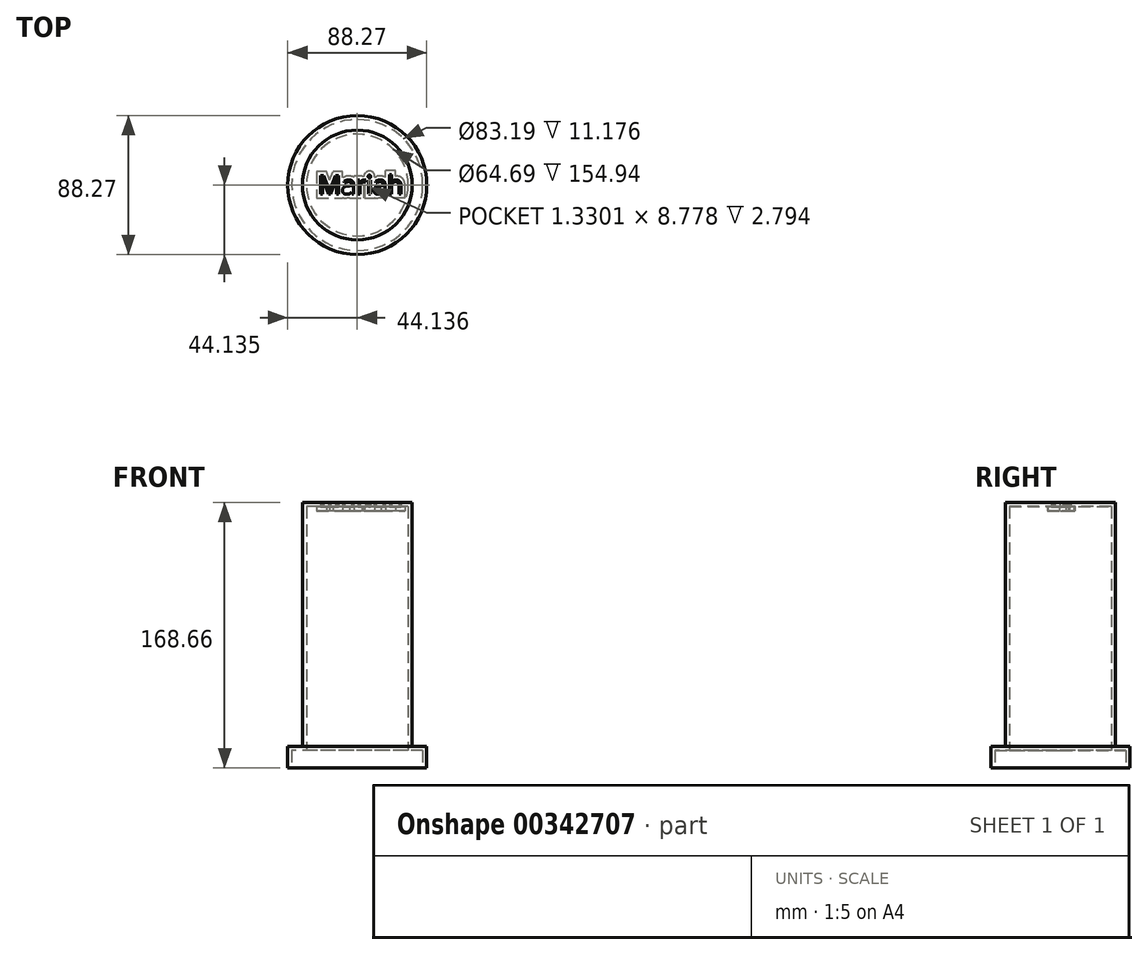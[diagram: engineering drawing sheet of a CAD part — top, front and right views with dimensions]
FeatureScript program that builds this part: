
annotation { "Feature Type Name" : "Feature", "Feature Type Description" : "" }
export const myFeature = defineFeature(function(context is Context, id is Id, definition is map)
    precondition{}
    {
        {
            var Q0;
            Q0=qCreatedBy(makeId("Top.planeOp"),FACE);
            var sketch = newSketch(context, id + "F0", { "sketchPlane" : qUnion([Q0])});
            skText(sketch, "E0", { "text": "Mariah", "fontName": "OpenSans-Regular.ttf"});
            skCircle(sketch, "E1", {"center": v(-33.62, 32.67) * mm, "radius": 34.89 * mm});
            skCircle(sketch, "E2", {"center": v(-33.62, 32.67) * mm, "radius": 44.14 * mm});
            const initialGuessF0  = {"E0": [-0.05858, 0.02693, 1, 0, 0.01181]};
            skSetInitialGuess(sketch, initialGuessF0);
            skSolve(sketch);
        }
        {
            var Q0;
            Q0 = qSketchRegion(id + "F0", true);
            var Q1;
            Q1=makeQuery(id+"F0.imprint","IMPRINT",FACE,{"disambiguationData":[TD([[makeQuery(id+"F0.imprint","IMPRINT",EDGE,{"derivedFrom":sQuery(id+"F0.wireOp",EDGE,"4TwiuxpI-l4dC-Yeu1-FSRf-eq53qfQSvJ1h")}),1.0]])]});
            extrude(context, id + "F1", {"entities" : qUnion([Q0, Q1]), "depth" : 6.35 * mm});
        }
        {
            var Q0;
            Q0 = qSketchRegion(id + "F0", true);
            var Q1;
            Q1=makeQuery(id+"F0.imprint","IMPRINT",FACE,{"disambiguationData":[TD([[makeQuery(id+"F0.imprint","IMPRINT",EDGE,{"derivedFrom":sQuery(id+"F0.wireOp",EDGE,"E0.sketch_text.stroke-0")}),1.0]])]});
            var Q2;
            Q2=makeQuery(id+"F0.imprint","IMPRINT",FACE,{"disambiguationData":[TD([[makeQuery(id+"F0.imprint","IMPRINT",EDGE,{"derivedFrom":sQuery(id+"F0.wireOp",EDGE,"E0.sketch_text.stroke-37")}),1.0]])]});
            var Q3;
            Q3=makeQuery(id+"F0.imprint","IMPRINT",FACE,{"disambiguationData":[TD([[makeQuery(id+"F0.imprint","IMPRINT",EDGE,{"derivedFrom":sQuery(id+"F0.wireOp",EDGE,"E0.sketch_text.stroke-18")}),-1.0]])]});
            var Q4;
            Q4=makeQuery(id+"F0.imprint","IMPRINT",FACE,{"disambiguationData":[TD([[makeQuery(id+"F0.imprint","IMPRINT",EDGE,{"derivedFrom":sQuery(id+"F0.wireOp",EDGE,"E0.sketch_text.stroke-0")}),-1.0]])]});
            var Q5;
            Q5=makeQuery(id+"F0.imprint","IMPRINT",FACE,{"disambiguationData":[TD([[makeQuery(id+"F0.imprint","IMPRINT",EDGE,{"derivedFrom":sQuery(id+"F0.wireOp",EDGE,"E0.sketch_text.stroke-45")}),-1.0]])]});
            var Q6;
            Q6=makeQuery(id+"F0.imprint","IMPRINT",FACE,{"disambiguationData":[TD([[makeQuery(id+"F0.imprint","IMPRINT",EDGE,{"derivedFrom":sQuery(id+"F0.wireOp",EDGE,"E0.sketch_text.stroke-58")}),-1.0]])]});
            var Q7;
            Q7=makeQuery(id+"F0.imprint","IMPRINT",FACE,{"disambiguationData":[TD([[makeQuery(id+"F0.imprint","IMPRINT",EDGE,{"derivedFrom":sQuery(id+"F0.wireOp",EDGE,"E0.sketch_text.stroke-62")}),-1.0]])]});
            var Q8;
            Q8=makeQuery(id+"F0.imprint","IMPRINT",FACE,{"disambiguationData":[TD([[makeQuery(id+"F0.imprint","IMPRINT",EDGE,{"derivedFrom":sQuery(id+"F0.wireOp",EDGE,"E0.sketch_text.stroke-70")}),-1.0]])]});
            var Q9;
            Q9=makeQuery(id+"F0.imprint","IMPRINT",FACE,{"disambiguationData":[TD([[makeQuery(id+"F0.imprint","IMPRINT",EDGE,{"derivedFrom":sQuery(id+"F0.wireOp",EDGE,"E0.sketch_text.stroke-89")}),1.0]])]});
            var Q10;
            Q10=makeQuery(id+"F0.imprint","IMPRINT",FACE,{"disambiguationData":[TD([[makeQuery(id+"F0.imprint","IMPRINT",EDGE,{"derivedFrom":sQuery(id+"F0.wireOp",EDGE,"E0.sketch_text.stroke-97")}),-1.0]])]});
            extrude(context, id + "F2", {"entities" : qUnion([Q0, Q1, Q2, Q3, Q4, Q5, Q6, Q7, Q8, Q9, Q10]), "operationType" : NewBodyOperationType.ADD, "depth" : 13.72 * mm});
        }
        {
            var Q0;
            Q0=makeQuery(id+"F0.imprint","IMPRINT",FACE,{"disambiguationData":[TD([[makeQuery(id+"F0.imprint","IMPRINT",EDGE,{"derivedFrom":sQuery(id+"F0.wireOp",EDGE,"E0.sketch_text.stroke-62")}),-1.0]])]});
            var Q1;
            Q1=makeQuery(id+"F0.imprint","IMPRINT",FACE,{"disambiguationData":[TD([[makeQuery(id+"F0.imprint","IMPRINT",EDGE,{"derivedFrom":sQuery(id+"F0.wireOp",EDGE,"E0.sketch_text.stroke-70")}),-1.0]])]});
            var Q2;
            Q2=makeQuery(id+"F0.imprint","IMPRINT",FACE,{"disambiguationData":[TD([[makeQuery(id+"F0.imprint","IMPRINT",EDGE,{"derivedFrom":sQuery(id+"F0.wireOp",EDGE,"E0.sketch_text.stroke-97")}),-1.0]])]});
            var Q3;
            Q3=makeQuery(id+"F0.imprint","IMPRINT",FACE,{"disambiguationData":[TD([[makeQuery(id+"F0.imprint","IMPRINT",EDGE,{"derivedFrom":sQuery(id+"F0.wireOp",EDGE,"E0.sketch_text.stroke-89")}),1.0]])]});
            var Q4;
            Q4=makeQuery(id+"F0.imprint","IMPRINT",FACE,{"disambiguationData":[TD([[makeQuery(id+"F0.imprint","IMPRINT",EDGE,{"derivedFrom":sQuery(id+"F0.wireOp",EDGE,"E0.sketch_text.stroke-58")}),-1.0]])]});
            var Q5;
            Q5=makeQuery(id+"F0.imprint","IMPRINT",FACE,{"disambiguationData":[TD([[makeQuery(id+"F0.imprint","IMPRINT",EDGE,{"derivedFrom":sQuery(id+"F0.wireOp",EDGE,"E0.sketch_text.stroke-45")}),-1.0]])]});
            var Q6;
            Q6=makeQuery(id+"F0.imprint","IMPRINT",FACE,{"disambiguationData":[TD([[makeQuery(id+"F0.imprint","IMPRINT",EDGE,{"derivedFrom":sQuery(id+"F0.wireOp",EDGE,"E0.sketch_text.stroke-18")}),-1.0]])]});
            var Q7;
            Q7=makeQuery(id+"F0.imprint","IMPRINT",FACE,{"disambiguationData":[TD([[makeQuery(id+"F0.imprint","IMPRINT",EDGE,{"derivedFrom":sQuery(id+"F0.wireOp",EDGE,"E0.sketch_text.stroke-37")}),1.0]])]});
            var Q8;
            Q8=makeQuery(id+"F0.imprint","IMPRINT",FACE,{"disambiguationData":[TD([[makeQuery(id+"F0.imprint","IMPRINT",EDGE,{"derivedFrom":sQuery(id+"F0.wireOp",EDGE,"E0.sketch_text.stroke-0")}),-1.0]])]});
            var Q9;
            Q9=makeQuery(id+"F0.imprint","IMPRINT",FACE,{"disambiguationData":[TD([[makeQuery(id+"F0.imprint","IMPRINT",EDGE,{"derivedFrom":sQuery(id+"F0.wireOp",EDGE,"E0.sketch_text.stroke-0")}),1.0]])]});
            extrude(context, id + "F3", {"entities" : qUnion([Q0, Q1, Q2, Q3, Q4, Q5, Q6, Q7, Q8, Q9]), "operationType" : NewBodyOperationType.ADD, "depth" : 165.86 * mm});
        }
        {
            var Q0;
            Q0=makeQuery(id+"F0.imprint","IMPRINT",FACE,{"disambiguationData":[TD([[makeQuery(id+"F0.imprint","IMPRINT",EDGE,{"derivedFrom":sQuery(id+"F0.wireOp",EDGE,"E0.sketch_text.stroke-0")}),1.0]])]});
            extrude(context, id + "F4", {"entities" : qUnion([Q0]), "operationType" : NewBodyOperationType.ADD, "depth" : 168.66 * mm, "hasSecondDirection" : true, "secondDirectionOppositeDirection" : false, "secondDirectionDepth" : 149.1 * mm});
        }
        {
            var Q1;
            Q1=makeQuery(id+"F4.opExtrude","CAP_FACE",FACE,{"disambiguationData":[OSD([sQuery(id+"F0.wireOp",EDGE,"E0.sketch_text.stroke-0"),sQuery(id+"F0.wireOp",EDGE,"E0.sketch_text.stroke-1"),sQuery(id+"F0.wireOp",EDGE,"E0.sketch_text.stroke-2"),sQuery(id+"F0.wireOp",EDGE,"E0.sketch_text.stroke-3"),sQuery(id+"F0.wireOp",EDGE,"E0.sketch_text.stroke-4"),sQuery(id+"F0.wireOp",EDGE,"E0.sketch_text.stroke-5"),sQuery(id+"F0.wireOp",EDGE,"E0.sketch_text.stroke-6"),sQuery(id+"F0.wireOp",EDGE,"E0.sketch_text.stroke-7"),sQuery(id+"F0.wireOp",EDGE,"E0.sketch_text.stroke-8"),sQuery(id+"F0.wireOp",EDGE,"E0.sketch_text.stroke-9"),sQuery(id+"F0.wireOp",EDGE,"E0.sketch_text.stroke-10"),sQuery(id+"F0.wireOp",EDGE,"E0.sketch_text.stroke-11"),sQuery(id+"F0.wireOp",EDGE,"E0.sketch_text.stroke-12"),sQuery(id+"F0.wireOp",EDGE,"E0.sketch_text.stroke-13"),sQuery(id+"F0.wireOp",EDGE,"E0.sketch_text.stroke-14"),sQuery(id+"F0.wireOp",EDGE,"E0.sketch_text.stroke-15"),sQuery(id+"F0.wireOp",EDGE,"E0.sketch_text.stroke-16"),sQuery(id+"F0.wireOp",EDGE,"E0.sketch_text.stroke-17"),sQuery(id+"F0.wireOp",EDGE,"E0.sketch_text.stroke-18"),sQuery(id+"F0.wireOp",EDGE,"E0.sketch_text.stroke-19"),sQuery(id+"F0.wireOp",EDGE,"E0.sketch_text.stroke-20"),sQuery(id+"F0.wireOp",EDGE,"E0.sketch_text.stroke-21"),sQuery(id+"F0.wireOp",EDGE,"E0.sketch_text.stroke-22"),sQuery(id+"F0.wireOp",EDGE,"E0.sketch_text.stroke-23"),sQuery(id+"F0.wireOp",EDGE,"E0.sketch_text.stroke-24"),sQuery(id+"F0.wireOp",EDGE,"E0.sketch_text.stroke-25"),sQuery(id+"F0.wireOp",EDGE,"E0.sketch_text.stroke-26"),sQuery(id+"F0.wireOp",EDGE,"E0.sketch_text.stroke-27"),sQuery(id+"F0.wireOp",EDGE,"E0.sketch_text.stroke-28"),sQuery(id+"F0.wireOp",EDGE,"E0.sketch_text.stroke-29"),sQuery(id+"F0.wireOp",EDGE,"E0.sketch_text.stroke-30"),sQuery(id+"F0.wireOp",EDGE,"E0.sketch_text.stroke-31"),sQuery(id+"F0.wireOp",EDGE,"E0.sketch_text.stroke-32"),sQuery(id+"F0.wireOp",EDGE,"E0.sketch_text.stroke-33"),sQuery(id+"F0.wireOp",EDGE,"E0.sketch_text.stroke-34"),sQuery(id+"F0.wireOp",EDGE,"E0.sketch_text.stroke-35"),sQuery(id+"F0.wireOp",EDGE,"E0.sketch_text.stroke-36"),sQuery(id+"F0.wireOp",EDGE,"E0.sketch_text.stroke-45"),sQuery(id+"F0.wireOp",EDGE,"E0.sketch_text.stroke-46"),sQuery(id+"F0.wireOp",EDGE,"E0.sketch_text.stroke-47"),sQuery(id+"F0.wireOp",EDGE,"E0.sketch_text.stroke-48"),sQuery(id+"F0.wireOp",EDGE,"E0.sketch_text.stroke-49"),sQuery(id+"F0.wireOp",EDGE,"E0.sketch_text.stroke-50"),sQuery(id+"F0.wireOp",EDGE,"E0.sketch_text.stroke-51"),sQuery(id+"F0.wireOp",EDGE,"E0.sketch_text.stroke-52"),sQuery(id+"F0.wireOp",EDGE,"E0.sketch_text.stroke-53"),sQuery(id+"F0.wireOp",EDGE,"E0.sketch_text.stroke-54"),sQuery(id+"F0.wireOp",EDGE,"E0.sketch_text.stroke-55"),sQuery(id+"F0.wireOp",EDGE,"E0.sketch_text.stroke-56"),sQuery(id+"F0.wireOp",EDGE,"E0.sketch_text.stroke-57"),sQuery(id+"F0.wireOp",EDGE,"E0.sketch_text.stroke-58"),sQuery(id+"F0.wireOp",EDGE,"E0.sketch_text.stroke-59"),sQuery(id+"F0.wireOp",EDGE,"E0.sketch_text.stroke-60"),sQuery(id+"F0.wireOp",EDGE,"E0.sketch_text.stroke-61"),sQuery(id+"F0.wireOp",EDGE,"E0.sketch_text.stroke-62"),sQuery(id+"F0.wireOp",EDGE,"E0.sketch_text.stroke-63"),sQuery(id+"F0.wireOp",EDGE,"E0.sketch_text.stroke-64"),sQuery(id+"F0.wireOp",EDGE,"E0.sketch_text.stroke-65"),sQuery(id+"F0.wireOp",EDGE,"E0.sketch_text.stroke-66"),sQuery(id+"F0.wireOp",EDGE,"E0.sketch_text.stroke-67"),sQuery(id+"F0.wireOp",EDGE,"E0.sketch_text.stroke-68"),sQuery(id+"F0.wireOp",EDGE,"E0.sketch_text.stroke-69"),sQuery(id+"F0.wireOp",EDGE,"E0.sketch_text.stroke-70"),sQuery(id+"F0.wireOp",EDGE,"E0.sketch_text.stroke-71"),sQuery(id+"F0.wireOp",EDGE,"E0.sketch_text.stroke-72"),sQuery(id+"F0.wireOp",EDGE,"E0.sketch_text.stroke-73"),sQuery(id+"F0.wireOp",EDGE,"E0.sketch_text.stroke-74"),sQuery(id+"F0.wireOp",EDGE,"E0.sketch_text.stroke-75"),sQuery(id+"F0.wireOp",EDGE,"E0.sketch_text.stroke-76"),sQuery(id+"F0.wireOp",EDGE,"E0.sketch_text.stroke-77"),sQuery(id+"F0.wireOp",EDGE,"E0.sketch_text.stroke-78"),sQuery(id+"F0.wireOp",EDGE,"E0.sketch_text.stroke-79"),sQuery(id+"F0.wireOp",EDGE,"E0.sketch_text.stroke-80"),sQuery(id+"F0.wireOp",EDGE,"E0.sketch_text.stroke-81"),sQuery(id+"F0.wireOp",EDGE,"E0.sketch_text.stroke-82"),sQuery(id+"F0.wireOp",EDGE,"E0.sketch_text.stroke-83"),sQuery(id+"F0.wireOp",EDGE,"E0.sketch_text.stroke-84"),sQuery(id+"F0.wireOp",EDGE,"E0.sketch_text.stroke-85"),sQuery(id+"F0.wireOp",EDGE,"E0.sketch_text.stroke-86"),sQuery(id+"F0.wireOp",EDGE,"E0.sketch_text.stroke-87"),sQuery(id+"F0.wireOp",EDGE,"E0.sketch_text.stroke-88"),sQuery(id+"F0.wireOp",EDGE,"E0.sketch_text.stroke-97"),sQuery(id+"F0.wireOp",EDGE,"E0.sketch_text.stroke-98"),sQuery(id+"F0.wireOp",EDGE,"E0.sketch_text.stroke-99"),sQuery(id+"F0.wireOp",EDGE,"E0.sketch_text.stroke-100"),sQuery(id+"F0.wireOp",EDGE,"E0.sketch_text.stroke-101"),sQuery(id+"F0.wireOp",EDGE,"E0.sketch_text.stroke-102"),sQuery(id+"F0.wireOp",EDGE,"E0.sketch_text.stroke-103"),sQuery(id+"F0.wireOp",EDGE,"E0.sketch_text.stroke-104"),sQuery(id+"F0.wireOp",EDGE,"E0.sketch_text.stroke-105"),sQuery(id+"F0.wireOp",EDGE,"E0.sketch_text.stroke-106"),sQuery(id+"F0.wireOp",EDGE,"E0.sketch_text.stroke-107"),sQuery(id+"F0.wireOp",EDGE,"E0.sketch_text.stroke-108"),sQuery(id+"F0.wireOp",EDGE,"E0.sketch_text.stroke-109"),sQuery(id+"F0.wireOp",EDGE,"E0.sketch_text.stroke-110"),sQuery(id+"F0.wireOp",EDGE,"E0.sketch_text.stroke-111"),sQuery(id+"F0.wireOp",EDGE,"E0.sketch_text.stroke-112"),sQuery(id+"F0.wireOp",EDGE,"E0.sketch_text.stroke-113"),sQuery(id+"F0.wireOp",EDGE,"E0.sketch_text.stroke-114"),sQuery(id+"F0.wireOp",EDGE,"E1")])],"isStart":false});
            var Q2;
            Q2=makeQuery(id+"F0.imprint","IMPRINT",FACE,{"disambiguationData":[TD([[makeQuery(id+"F0.imprint","IMPRINT",EDGE,{"derivedFrom":sQuery(id+"F0.wireOp",EDGE,"E1")}),-1.0]])]});
            var Q3;
            Q3=makeQuery(id+"F4.opExtrude","CAP_EDGE",EDGE,{"disambiguationData":[OSD([sQuery(id+"F0.wireOp",EDGE,"E1")])],"isStart":false});
            var Q4;
            Q4=sQuery(id+"F0.wireOp",EDGE,"E2");
            loft(context, id + "F5", {"bodyType" : ToolBodyType.SURFACE, "operationType" : NewBodyOperationType.ADD, "sheetProfilesArray" : [{ "sheetProfileEntities" : qUnion([Q1]) }, { "sheetProfileEntities" : qUnion([Q2]) }], "wireProfilesArray" : [{ "wireProfileEntities" : qUnion([Q3]) }, { "wireProfileEntities" : qUnion([Q4]) }]});
        }
        {
            var Q0;
            {var subQ0=sQuery(id+"F0.wireOp",EDGE,"E2");Q0=makeQuery(id+"F2.boolean.opBoolean","MERGE",FACE,{"derivedFrom":[makeQuery(id+"F1.opExtrude","CAP_FACE",FACE,{"disambiguationData":[OSD([sQuery(id+"F0.wireOp",EDGE,"E1"),subQ0])],"isStart":true}),makeQuery(id+"F2.opExtrude","CAP_FACE",FACE,{"disambiguationData":[OSD([subQ0])],"isStart":true})]});}
            shell(context, id + "F6", {"entities" : qUnion([Q0]), "thickness" : 2.54 * mm});
        }
    });
